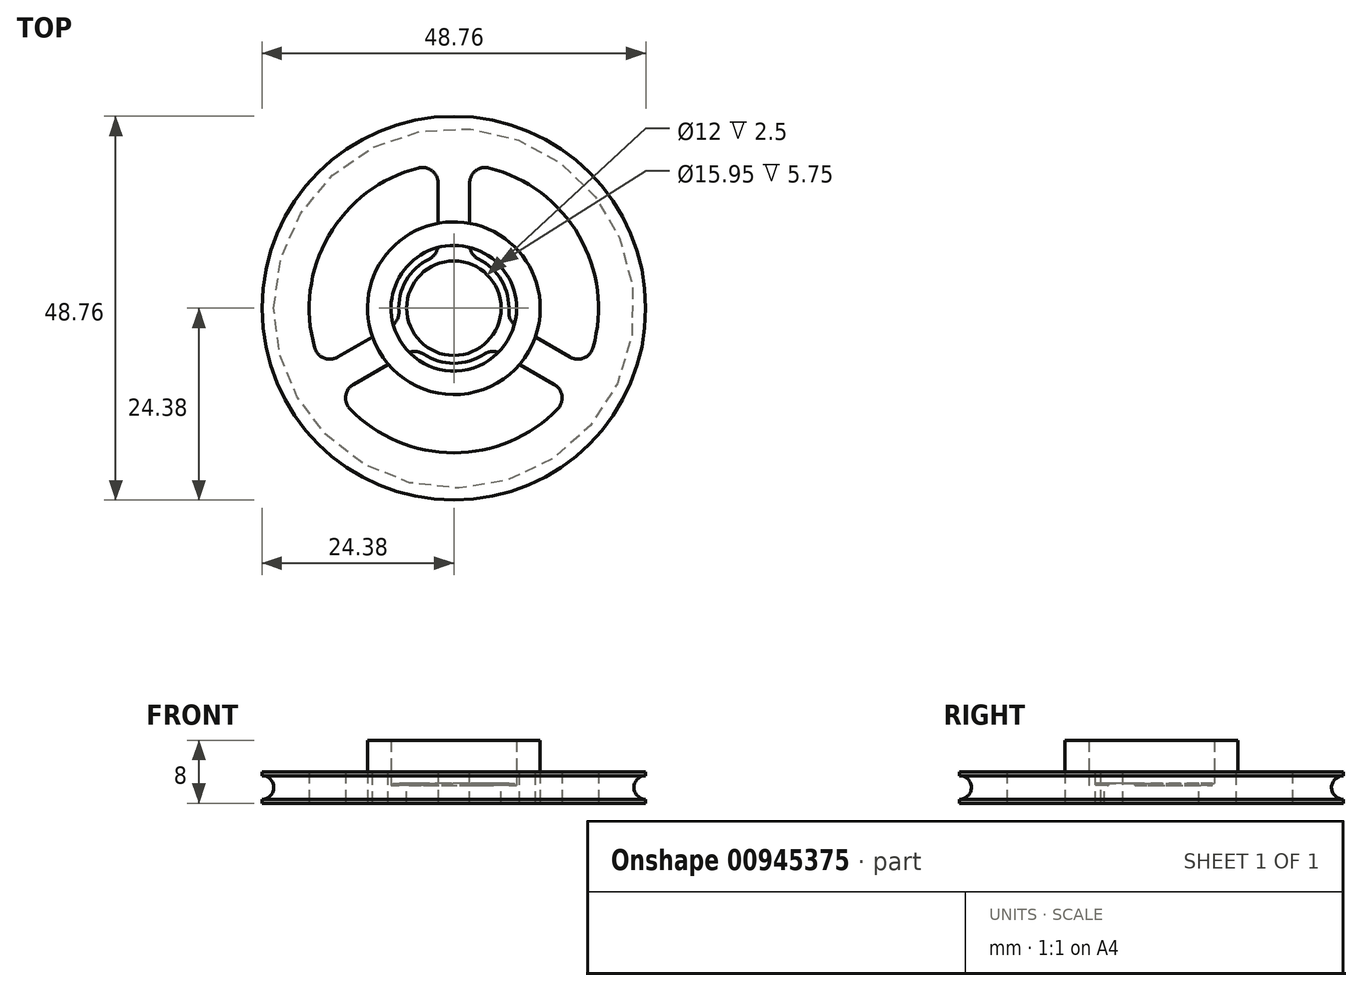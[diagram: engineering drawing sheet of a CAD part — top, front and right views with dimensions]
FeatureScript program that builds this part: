
annotation { "Feature Type Name" : "Feature", "Feature Type Description" : "" }
export const myFeature = defineFeature(function(context is Context, id is Id, definition is map)
    precondition{}
    {
        {
            var Q0;
            Q0=qCreatedBy(makeId("Top.planeOp"),FACE);
            var sketch = newSketch(context, id + "F0", { "sketchPlane" : qUnion([Q0])});
            skCircle(sketch, "E0", {"center": v(0, 0) * mm, "radius": 24.38 * mm});
            skArc(sketch, "E1", {"start": v(-3.11, 6.27) * mm, "mid": v(-6.06, 3.5) * mm, "end": v(-6.99, -0.44) * mm});
            skArc(sketch, "E2.0", {"start": v(-4.49, 17.82) * mm, "mid": v(-15.91, 9.19) * mm, "end": v(-17.68, -5.02) * mm});
            skLineSegment(sketch, "E3.0", {"start": v(2, 15.88) * mm, "end": v(2, 8.06) * mm});
            skLineSegment(sketch, "E4.0", {"start": v(-2, 15.88) * mm, "end": v(-2, 8.06) * mm});
            skPoint(sketch, "E5.orphan", {"position": v(0, 20.13) * mm});
            skPoint(sketch, "E6.visualSharp", {"position": v(-2, 18.27) * mm});
            skArc(sketch, "E6.filletArc", {"start": v(-2, 15.88) * mm, "mid": v(-2.77, 17.46) * mm, "end": v(-4.49, 17.82) * mm});
            skPoint(sketch, "E7.visualSharp", {"position": v(2, 18.27) * mm});
            skArc(sketch, "E7.filletArc", {"start": v(4.49, 17.82) * mm, "mid": v(2.77, 17.46) * mm, "end": v(2, 15.88) * mm});
            skPoint(sketch, "E8.visualSharp", {"position": v(2, 6.7) * mm});
            skArc(sketch, "E8.filletArc", {"start": v(2, 8.06) * mm, "mid": v(2.3, 7) * mm, "end": v(3.11, 6.27) * mm});
            skPoint(sketch, "E9.visualSharp", {"position": v(-2, 6.7) * mm});
            skArc(sketch, "E9.filletArc", {"start": v(-3.11, 6.27) * mm, "mid": v(-2.3, 7) * mm, "end": v(-2, 8.06) * mm});
            skLineSegment(sketch, "E10.1.0", {"start": v(-14.75, -6.2) * mm, "end": v(-7.98, -2.3) * mm});
            skArc(sketch, "E10.1.1", {"start": v(-17.68, -5.02) * mm, "mid": v(-16.5, -6.33) * mm, "end": v(-14.75, -6.2) * mm});
            skArc(sketch, "E10.1.2", {"start": v(-12.75, -9.67) * mm, "mid": v(-13.73, -11.13) * mm, "end": v(-13.19, -12.8) * mm});
            skLineSegment(sketch, "E10.1.3", {"start": v(-12.75, -9.67) * mm, "end": v(-5.98, -5.76) * mm});
            skArc(sketch, "E10.1.4", {"start": v(-3.87, -5.83) * mm, "mid": v(-4.92, -5.5) * mm, "end": v(-5.98, -5.76) * mm});
            skArc(sketch, "E10.1.5", {"start": v(-7.98, -2.3) * mm, "mid": v(-7.22, -1.51) * mm, "end": v(-6.99, -0.44) * mm});
            skLineSegment(sketch, "E10.2.0", {"start": v(12.75, -9.67) * mm, "end": v(5.98, -5.76) * mm});
            skArc(sketch, "E10.2.1", {"start": v(13.19, -12.8) * mm, "mid": v(13.73, -11.13) * mm, "end": v(12.75, -9.67) * mm});
            skArc(sketch, "E10.2.2", {"start": v(14.75, -6.2) * mm, "mid": v(16.5, -6.33) * mm, "end": v(17.68, -5.02) * mm});
            skLineSegment(sketch, "E10.2.3", {"start": v(14.75, -6.2) * mm, "end": v(7.98, -2.3) * mm});
            skArc(sketch, "E10.2.4", {"start": v(6.99, -0.44) * mm, "mid": v(7.22, -1.51) * mm, "end": v(7.98, -2.3) * mm});
            skArc(sketch, "E10.2.5", {"start": v(5.98, -5.76) * mm, "mid": v(4.92, -5.5) * mm, "end": v(3.87, -5.83) * mm});
            skArc(sketch, "E11.trimOffspring", {"start": v(-3.87, -5.83) * mm, "mid": v(0, -7) * mm, "end": v(3.87, -5.83) * mm});
            skArc(sketch, "E12.trimOffspring", {"start": v(6.99, -0.44) * mm, "mid": v(6.06, 3.5) * mm, "end": v(3.11, 6.27) * mm});
            skArc(sketch, "E13.trimOffspring", {"start": v(17.68, -5.02) * mm, "mid": v(15.91, 9.19) * mm, "end": v(4.49, 17.82) * mm});
            skArc(sketch, "E14.trimOffspring", {"start": v(-13.19, -12.8) * mm, "mid": v(0, -18.38) * mm, "end": v(13.19, -12.8) * mm});
            skSolve(sketch);
        }
        {
            var Q0;
            Q0=makeQuery(id+"F0.imprint","IMPRINT",FACE,{"disambiguationData":[TD([[makeQuery(id+"F0.imprint","IMPRINT",EDGE,{"derivedFrom":sQuery(id+"F0.wireOp",EDGE,"E0")}),1.0]])]});
            extrude(context, id + "F1", {"entities" : qUnion([Q0]), "depth" : 4 * mm, "offsetDistance" : 25.4 * mm});
        }
        {
            var Q0;
            Q0=makeQuery(id+"F1.opExtrude","CAP_FACE",FACE,{"disambiguationData":[OSD([sQuery(id+"F0.wireOp",EDGE,"E0"),sQuery(id+"F0.wireOp",EDGE,"n39IqKt5-bk1q-LU1x-fgod-8OyBNiFTd7FZ")])],"isStart":false});
            var sketch = newSketch(context, id + "F2", { "sketchPlane" : qUnion([Q0])});
            skCircle(sketch, "E15", {"center": v(0, 0) * mm, "radius": 7.97 * mm});
            skCircle(sketch, "E16.0", {"center": v(0, 0) * mm, "radius": 10.97 * mm});
            skSolve(sketch);
        }
        {
            var Q0;
            Q0=qSketchRegion(id+"F2",true);
            extrude(context, id + "F3", {"entities" : qUnion([Q0]), "operationType" : NewBodyOperationType.ADD, "depth" : 4 * mm, "offsetDistance" : 25.4 * mm});
        }
        {
            var Q0;
            Q0=makeQuery(id+"F3.boolean.opBoolean","SPLIT",FACE,{"disambiguationData":[TD([makeQuery(id+"F3.opExtrude","SWEPT_FACE",FACE,{"disambiguationData":[OSD([sQuery(id+"F2.wireOp",EDGE,"E15")])]})])],"derivedFrom":makeQuery(id+"F1.opExtrude","CAP_FACE",FACE,{"disambiguationData":[OSD([sQuery(id+"F0.wireOp",EDGE,"E0")])],"isStart":false})});
            var sketch = newSketch(context, id + "F4", { "sketchPlane" : qUnion([Q0])});
            skCircle(sketch, "E17", {"center": v(0, 0) * mm, "radius": 6 * mm});
            skSolve(sketch);
        }
        {
            var Q0;
            Q0=makeQuery(id+"F4.imprint","IMPRINT",FACE,{"disambiguationData":[TD([[makeQuery(id+"F4.imprint","IMPRINT",EDGE,{"derivedFrom":sQuery(id+"F4.wireOp",EDGE,"E17")}),1.0]])]});
            extrude(context, id + "F5", {"entities" : qUnion([Q0]), "operationType" : NewBodyOperationType.REMOVE, "flatOperationType" : FlatOperationType.REMOVE, "oppositeDirection" : true, "depth" : 9 * mm, "offsetDistance" : 25.4 * mm, "domain" : OperationDomain.MODEL});
        }
        {
            var Q0;
            Q0=qCreatedBy(makeId("Front.planeOp"),FACE);
            var sketch = newSketch(context, id + "F6", { "sketchPlane" : qUnion([Q0])});
            skCircle(sketch, "E18", {"center": v(-24.38, 2) * mm, "radius": 1.5 * mm});
            skLineSegment(sketch, "E19.bottom", {"start": v(-22.88, 0.65) * mm, "end": v(-25.02, 0.65) * mm});
            skLineSegment(sketch, "E19.top", {"start": v(-22.88, 3.35) * mm, "end": v(-25.02, 3.35) * mm});
            skLineSegment(sketch, "E19.left", {"start": v(-22.88, 0.65) * mm, "end": v(-22.88, 3.35) * mm});
            skLineSegment(sketch, "E19.right", {"start": v(-25.73, 1.35) * mm, "end": v(-25.73, 2.65) * mm});
            skLineSegment(sketch, "E20", {"start": v(0, 19.1) * mm, "end": v(0, -12.61) * mm, "construction": true});
            skLineSegment(sketch, "E21", {"start": v(-24.37, 3.35) * mm, "end": v(-22.88, 2) * mm});
            skLineSegment(sketch, "E22", {"start": v(-22.88, 2) * mm, "end": v(-24.38, 0.65) * mm});
            skLineSegment(sketch, "E23", {"start": v(-24.38, 0.65) * mm, "end": v(-24.37, 3.35) * mm});
            skSolve(sketch);
        }
        {
            var Q0;
            {var subQ0=sQuery(id+"F6.wireOp",EDGE,"E19.top");var subQ1=sQuery(id+"F6.wireOp",EDGE,"E18");var subQ2=makeQuery(id+"F6.imprint","INTERSECT",VERTEX,{"disambiguationData":[OD(0.0)],"derivedFrom":[subQ1,subQ0]});Q0=makeQuery(id+"F6.imprint","IMPRINT",FACE,{"disambiguationData":[TD([[makeQuery(id+"F6.imprint","IMPRINT",EDGE,{"disambiguationData":[TD([[subQ2,1.0]])],"derivedFrom":subQ1}),1.0]])]});}
            var Q1;
            {var subQ0=sQuery(id+"F6.wireOp",EDGE,"E19.bottom");var subQ1=sQuery(id+"F6.wireOp",EDGE,"E18");var subQ2=makeQuery(id+"F6.imprint","INTERSECT",VERTEX,{"disambiguationData":[OD(0.0)],"derivedFrom":[subQ1,subQ0]});Q1=makeQuery(id+"F6.imprint","IMPRINT",FACE,{"disambiguationData":[TD([[makeQuery(id+"F6.imprint","IMPRINT",EDGE,{"disambiguationData":[TD([[subQ2,-1.0]])],"derivedFrom":subQ1}),1.0]])]});}
            var Q2;
            {var subQ4=sQuery(id+"F6.wireOp",EDGE,"E19.right");Q2=makeQuery(id+"F6.imprint","IMPRINT",FACE,{"disambiguationData":[TD([[makeQuery(id+"F6.imprint","IMPRINT",EDGE,{"derivedFrom":subQ4}),-1.0]])]});}
            var Q3;
            {var subQ0=sQuery(id+"F6.wireOp",EDGE,"E21");Q3=makeQuery(id+"F6.imprint","IMPRINT",FACE,{"disambiguationData":[TD([[makeQuery(id+"F6.imprint","IMPRINT",EDGE,{"derivedFrom":subQ0}),1.0]])]});}
            var Q4;
            Q4=makeQuery(id+"F6.imprint","IMPRINT",FACE,{"disambiguationData":[TD([[makeQuery(id+"F6.imprint","IMPRINT",EDGE,{"derivedFrom":sQuery(id+"F6.wireOp",EDGE,"E21")}),-1.0]])]});
            var Q5;
            {var subQ0=sQuery(id+"F6.wireOp",EDGE,"E22");Q5=makeQuery(id+"F6.imprint","IMPRINT",FACE,{"disambiguationData":[TD([[makeQuery(id+"F6.imprint","IMPRINT",EDGE,{"derivedFrom":subQ0}),1.0]])]});}
            var Q6;
            Q6=sQuery(id+"F6.wireOp",EDGE,"E20");
            revolve(context, id + "F7", {"operationType" : NewBodyOperationType.REMOVE, "surfaceOperationType" : NewSurfaceOperationType.NEW, "entities" : qUnion([Q0, Q1, Q2, Q3, Q4, Q5]), "axis" : qUnion([Q6]), "revolveType" : RevolveType.FULL, "oppositeDirection" : true});
        }
        {
            var Q0;
            Q0=makeQuery(id+"F3.boolean.opBoolean","SPLIT",FACE,{"disambiguationData":[TD([makeQuery(id+"F3.opExtrude","SWEPT_FACE",FACE,{"disambiguationData":[OSD([sQuery(id+"F2.wireOp",EDGE,"E15")])]})])],"derivedFrom":makeQuery(id+"F1.opExtrude","CAP_FACE",FACE,{"disambiguationData":[OSD([sQuery(id+"F0.wireOp",EDGE,"E0")])],"isStart":false})});
            extrude(context, id + "F8", {"entities" : qUnion([Q0]), "operationType" : NewBodyOperationType.REMOVE, "flatOperationType" : FlatOperationType.REMOVE, "oppositeDirection" : true, "depth" : 1.5 * mm, "offsetDistance" : 25 * mm, "domain" : OperationDomain.MODEL});
        }
        {
            var Q0;
            {var subQ0=makeQuery(id+"F1.opExtrude","CAP_EDGE",EDGE,{"disambiguationData":[OSD([sQuery(id+"F0.wireOp",EDGE,"E9.filletArc")])],"isStart":false});var subQ5=sQuery(id+"F2.wireOp",EDGE,"E15");var subQ6=makeQuery(id+"F2.imprint","INTERSECT",VERTEX,{"derivedFrom":[subQ0,subQ5]});Q0=makeQuery(id+"F2.imprint","IMPRINT",FACE,{"disambiguationData":[TD([[makeQuery(id+"F2.imprint","IMPRINT",EDGE,{"disambiguationData":[TD([[subQ6,-1.0]])],"derivedFrom":subQ5}),-1.0]])]});}
            var Q1;
            {var subQ0=makeQuery(id+"F1.opExtrude","CAP_EDGE",EDGE,{"disambiguationData":[OSD([sQuery(id+"F0.wireOp",EDGE,"E10.1.4")])],"isStart":false});var subQ3=sQuery(id+"F2.wireOp",EDGE,"E15");var subQ4=makeQuery(id+"F2.imprint","INTERSECT",VERTEX,{"derivedFrom":[subQ0,subQ3]});Q1=makeQuery(id+"F2.imprint","IMPRINT",FACE,{"disambiguationData":[TD([[makeQuery(id+"F2.imprint","IMPRINT",EDGE,{"disambiguationData":[TD([[subQ4,-1.0]])],"derivedFrom":subQ3}),-1.0]])]});}
            var Q2;
            {var subQ0=makeQuery(id+"F1.opExtrude","CAP_EDGE",EDGE,{"disambiguationData":[OSD([sQuery(id+"F0.wireOp",EDGE,"E8.filletArc")])],"isStart":false});var subQ3=sQuery(id+"F2.wireOp",EDGE,"E15");var subQ4=makeQuery(id+"F2.imprint","INTERSECT",VERTEX,{"derivedFrom":[subQ0,subQ3]});Q2=makeQuery(id+"F2.imprint","IMPRINT",FACE,{"disambiguationData":[TD([[makeQuery(id+"F2.imprint","IMPRINT",EDGE,{"disambiguationData":[TD([[subQ4,1.0]])],"derivedFrom":subQ3}),-1.0]])]});}
            extrude(context, id + "F9", {"entities" : qUnion([Q0, Q1, Q2]), "operationType" : NewBodyOperationType.ADD, "oppositeDirection" : true, "depth" : 4 * mm, "offsetDistance" : 25 * mm});
        }
        {
            var Q0;
            Q0=qCreatedBy(makeId("Top.planeOp"),FACE);
            var sketch = newSketch(context, id + "F10", { "sketchPlane" : qUnion([Q0])});
            skCircle(sketch, "E24", {"center": v(0, 0) * mm, "radius": 6 * mm});
            skCircle(sketch, "E25", {"center": v(0, 0) * mm, "radius": 8 * mm});
            skSolve(sketch);
        }
        {
            var Q0;
            Q0 = qSketchRegion(id + "F10", true);
            extrude(context, id + "F11", {"entities" : qUnion([Q0]), "operationType" : NewBodyOperationType.ADD, "flatOperationType" : FlatOperationType.REMOVE, "depth" : 2.25 * mm, "offsetDistance" : 25 * mm, "domain" : OperationDomain.MODEL});
        }
    });
